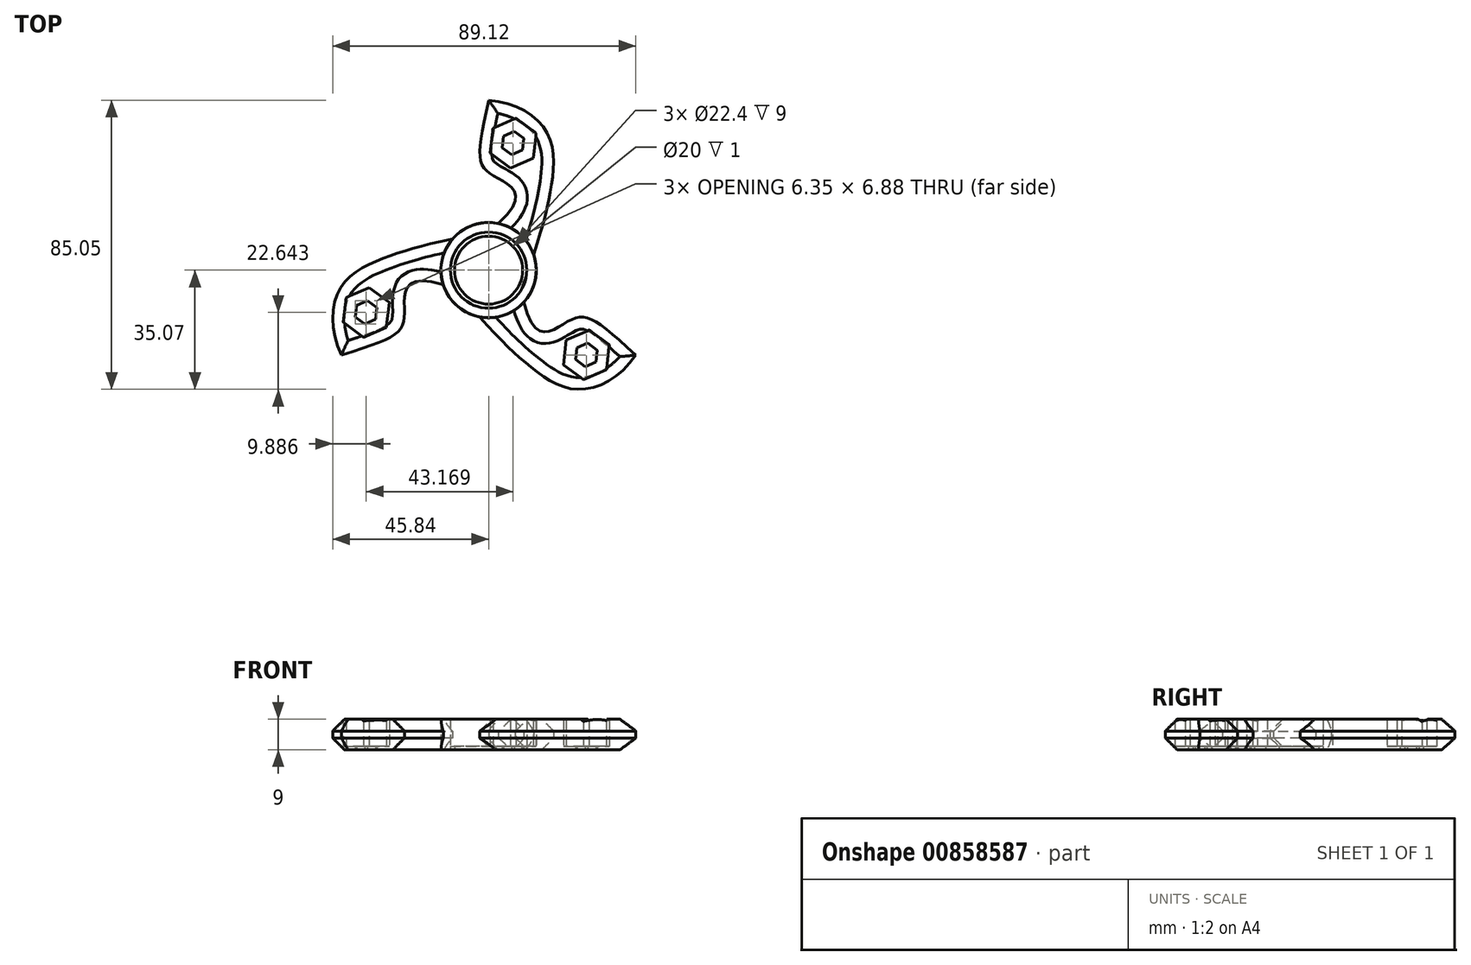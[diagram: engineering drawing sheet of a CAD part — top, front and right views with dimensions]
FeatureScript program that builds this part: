
annotation { "Feature Type Name" : "Feature", "Feature Type Description" : "" }
export const myFeature = defineFeature(function(context is Context, id is Id, definition is map)
    precondition{}
    {
        {
            var Q0;
            Q0=qCreatedBy(makeId("Top.planeOp"),FACE);
            var sketch = newSketch(context, id + "F0", { "sketchPlane" : qUnion([Q0])});
            skCircle(sketch, "E0", {"center": v(0, 0) * mm, "radius": 11.2 * mm});
            skLineSegment(sketch, "E1", {"start": v(0, 0) * mm, "end": v(0, 49.98) * mm, "construction": true});
            skLineSegment(sketch, "E2", {"start": v(0, 0) * mm, "end": v(63.41, -36.61) * mm, "construction": true});
            skFitSpline(sketch, "E3", {"points": [v(9.7, -5.6) * mm, v(18.36, 24.35) * mm, v(17.4, 39.97) * mm, v(0, 49.98) * mm], "startDerivative": vector(42.32, 118.32) * mm, "endDerivative": vector(-76.17, 5.67) * mm});
            skFitSpline(sketch, "E4", {"points": [v(0, 11.2) * mm, v(1.2, 27.86) * mm, v(0, 49.98) * mm], "startDerivative": vector(93.3, 74.93) * mm, "endDerivative": vector(18.94, 86.2) * mm});
            skCircle(sketch, "E5", {"center": v(0, 0) * mm, "radius": 14 * mm});
            skCircle(sketch, "E6.cCircle", {"center": v(7.21, 37.35) * mm, "radius": 6.37 * mm, "construction": true});
            skLineSegment(sketch, "E6.0", {"start": v(8.04, 44.66) * mm, "end": v(13.96, 40.29) * mm});
            skLineSegment(sketch, "E6.1", {"start": v(13.96, 40.29) * mm, "end": v(13.13, 32.98) * mm});
            skLineSegment(sketch, "E6.2", {"start": v(13.13, 32.98) * mm, "end": v(6.39, 30.04) * mm});
            skLineSegment(sketch, "E6.3", {"start": v(6.39, 30.04) * mm, "end": v(0.47, 34.41) * mm});
            skLineSegment(sketch, "E6.4", {"start": v(0.47, 34.41) * mm, "end": v(1.3, 41.72) * mm});
            skLineSegment(sketch, "E6.5", {"start": v(1.3, 41.72) * mm, "end": v(8.04, 44.66) * mm});
            skPoint(sketch, "E6.0.midPoint", {"position": v(11, 42.47) * mm});
            skCircle(sketch, "E7", {"center": v(0, 0) * mm, "radius": 10 * mm});
            skCircle(sketch, "E8.cCircle", {"center": v(7.21, 37.35) * mm, "radius": 3 * mm, "construction": true});
            skLineSegment(sketch, "E8.0", {"start": v(10.4, 38.73) * mm, "end": v(10, 35.3) * mm});
            skLineSegment(sketch, "E8.1", {"start": v(10, 35.3) * mm, "end": v(6.82, 33.9) * mm});
            skLineSegment(sketch, "E8.2", {"start": v(6.82, 33.9) * mm, "end": v(4.04, 35.97) * mm});
            skLineSegment(sketch, "E8.3", {"start": v(4.04, 35.97) * mm, "end": v(4.43, 39.4) * mm});
            skLineSegment(sketch, "E8.4", {"start": v(4.43, 39.4) * mm, "end": v(7.6, 40.8) * mm});
            skLineSegment(sketch, "E8.5", {"start": v(7.6, 40.8) * mm, "end": v(10.4, 38.73) * mm});
            skPoint(sketch, "E8.0.midPoint", {"position": v(10.2, 37.01) * mm});
            skLineSegment(sketch, "E9", {"start": v(0, 0) * mm, "end": v(68.43, 0) * mm, "construction": true});
            skLineSegment(sketch, "E10", {"start": v(0.47, 34.41) * mm, "end": v(13.96, 40.29) * mm, "construction": true});
            skSolve(sketch);
        }
        {
            var Q0;
            Q0=qSketchRegion(id+"F0",true);
            extrude(context, id + "F1", {"entities" : qUnion([Q0]), "depth" : 9 * mm, "offsetDistance" : 25 * mm});
        }
        {
            var Q0;
            Q0=makeQuery(id+"F0.imprint","IMPRINT",FACE,{"disambiguationData":[TD([[makeQuery(id+"F0.imprint","IMPRINT",EDGE,{"derivedFrom":sQuery(id+"F0.wireOp",EDGE,"E7")}),-1.0]])]});
            extrude(context, id + "F2", {"entities" : qUnion([Q0]), "depth" : 1 * mm, "offsetDistance" : 25 * mm});
        }
        {
            var Q0;
            Q0=makeQuery(id+"F0.imprint","IMPRINT",FACE,{"disambiguationData":[TD([[makeQuery(id+"F0.imprint","IMPRINT",EDGE,{"derivedFrom":sQuery(id+"F0.wireOp",EDGE,"E6.0")}),-1.0]])]});
            var Q1;
            Q1=makeQuery(id+"F0.imprint","IMPRINT",FACE,{"disambiguationData":[TD([[makeQuery(id+"F0.imprint","IMPRINT",EDGE,{"derivedFrom":sQuery(id+"F0.wireOp",EDGE,"e9405604-b3fd-474f-b84a-674374f038b5.0.1.0")}),-1.0]])]});
            var Q2;
            Q2=makeQuery(id+"F0.imprint","IMPRINT",FACE,{"disambiguationData":[TD([[makeQuery(id+"F0.imprint","IMPRINT",EDGE,{"derivedFrom":sQuery(id+"F0.wireOp",EDGE,"13bc22e7-b4a5-4678-b76a-06c36775fb35.0")}),-1.0]])]});
            extrude(context, id + "F3", {"entities" : qUnion([Q0, Q1, Q2]), "operationType" : NewBodyOperationType.ADD, "depth" : 1.08 * mm, "offsetDistance" : 25 * mm});
        }
        {
            var Q0;
            Q0=qCreatedBy(makeId("Front.planeOp"),FACE);
            var sketch = newSketch(context, id + "F4", { "sketchPlane" : qUnion([Q0])});
            skLineSegment(sketch, "E11", {"start": v(0, 0) * mm, "end": v(0, 39.09) * mm, "construction": true});
            skSolve(sketch);
        }
        {
            var Q0;
            Q0=makeQuery(id+"F1.opExtrude","CAP_EDGE",EDGE,{"disambiguationData":[OSD([sQuery(id+"F0.wireOp",EDGE,"E4")])],"isStart":true});
            var Q1;
            Q1=makeQuery(id+"F1.opExtrude","CAP_EDGE",EDGE,{"disambiguationData":[OSD([sQuery(id+"F0.wireOp",EDGE,"E3")])],"isStart":true});
            var Q2;
            Q2=makeQuery(id+"F1.opExtrude","CAP_EDGE",EDGE,{"disambiguationData":[OSD([sQuery(id+"F0.wireOp",EDGE,"E4")])],"isStart":false});
            var Q3;
            Q3=makeQuery(id+"F1.opExtrude","CAP_EDGE",EDGE,{"disambiguationData":[OSD([sQuery(id+"F0.wireOp",EDGE,"E3")])],"isStart":false});
            chamfer(context, id + "F5", {"entities" : qUnion([Q0, Q1, Q2, Q3]), "width" : 3.47 * mm, "tangentPropagation" : true});
        }
        {
            var Q0;
            Q0=makeQuery(id+"F1.opExtrude","SWEPT_BODY",BODY,{"disambiguationData":[OSD([sQuery(id+"F0.wireOp",EDGE,"E0"),sQuery(id+"F0.wireOp",EDGE,"E3"),sQuery(id+"F0.wireOp",EDGE,"E4"),sQuery(id+"F0.wireOp",EDGE,"E5"),sQuery(id+"F0.wireOp",EDGE,"E6.0"),sQuery(id+"F0.wireOp",EDGE,"E6.1"),sQuery(id+"F0.wireOp",EDGE,"E6.2"),sQuery(id+"F0.wireOp",EDGE,"E6.3"),sQuery(id+"F0.wireOp",EDGE,"E6.4"),sQuery(id+"F0.wireOp",EDGE,"E6.5"),sQuery(id+"F0.wireOp",EDGE,"e9405604-b3fd-474f-b84a-674374f038b5.0.1.0"),sQuery(id+"F0.wireOp",EDGE,"e9405604-b3fd-474f-b84a-674374f038b5.0.1.1"),sQuery(id+"F0.wireOp",EDGE,"e9405604-b3fd-474f-b84a-674374f038b5.0.1.2"),sQuery(id+"F0.wireOp",EDGE,"e9405604-b3fd-474f-b84a-674374f038b5.0.1.3"),sQuery(id+"F0.wireOp",EDGE,"e9405604-b3fd-474f-b84a-674374f038b5.0.1.4"),sQuery(id+"F0.wireOp",EDGE,"e9405604-b3fd-474f-b84a-674374f038b5.0.1.5")])]});
            var Q1;
            Q1=sQuery(id+"F4.wireOp",EDGE,"E11");
            circularPattern(context, id + "F6", {"entities" : qUnion([Q0]), "axis" : qUnion([Q1]), "angle" : 360 * degree, "instanceCount" : 3, "equalSpace" : true});
        }
    });
